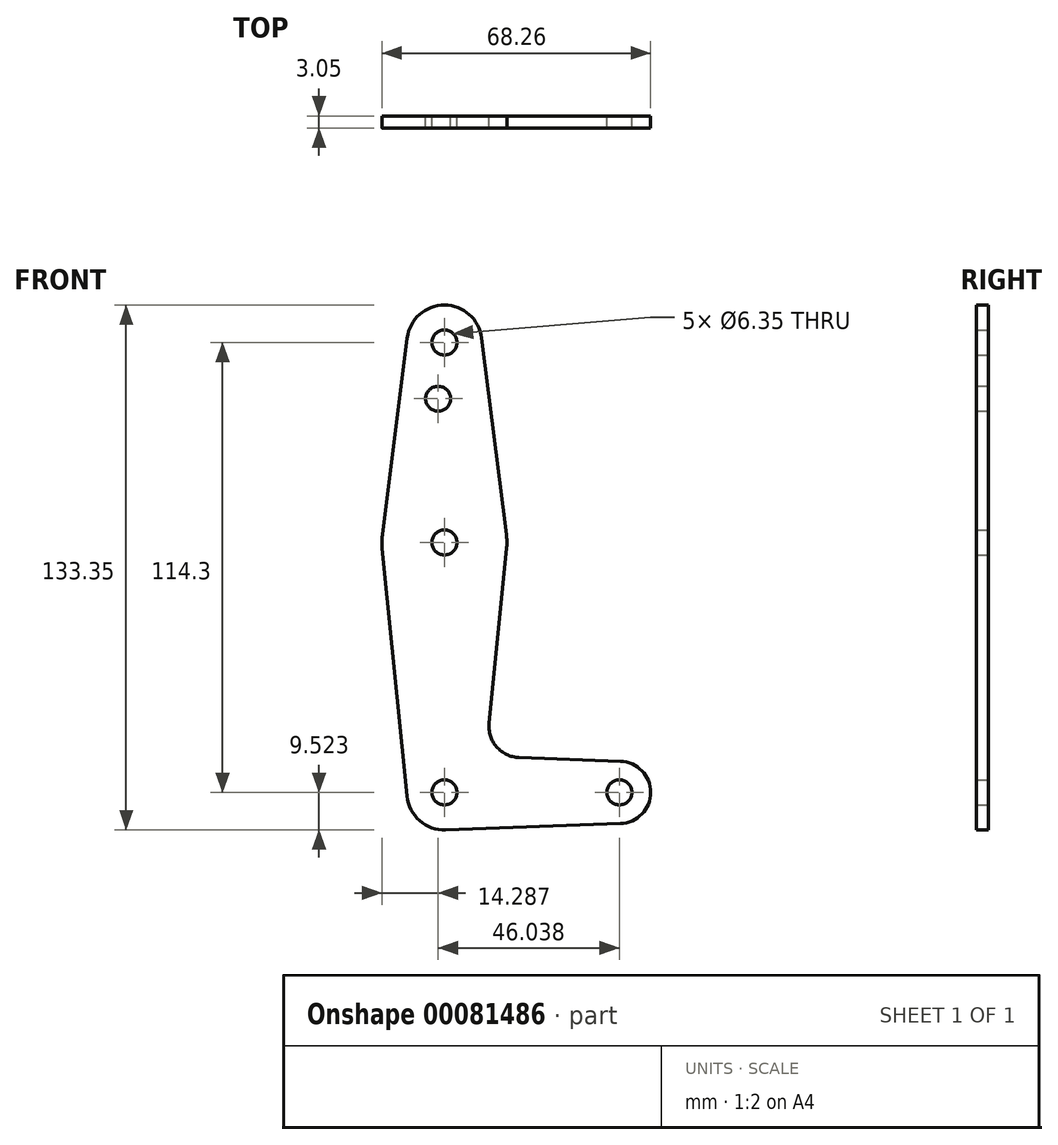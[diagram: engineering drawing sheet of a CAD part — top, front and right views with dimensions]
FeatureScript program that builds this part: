
annotation { "Feature Type Name" : "Feature", "Feature Type Description" : "" }
export const myFeature = defineFeature(function(context is Context, id is Id, definition is map)
    precondition{}
    {
        {
            var Q0;
            Q0=qCreatedBy(makeId("Front.planeOp"),FACE);
            var sketch = newSketch(context, id + "F0", { "sketchPlane" : qUnion([Q0])});
            skLineSegment(sketch, "E0", {"start": v(-60.13, 49.11) * mm, "end": v(-60.13, -65.19) * mm, "construction": true});
            skPoint(sketch, "E1.center.orphan", {"position": v(-60.13, -8.04) * mm});
            skCircle(sketch, "E2", {"center": v(-60.13, -1.69) * mm, "radius": 15.88 * mm});
            skCircle(sketch, "E3", {"center": v(-60.13, -65.19) * mm, "radius": 9.53 * mm});
            skLineSegment(sketch, "E4", {"start": v(-60.13, -65.19) * mm, "end": v(-15.68, -65.19) * mm, "construction": true});
            skCircle(sketch, "E5", {"center": v(-15.68, -65.19) * mm, "radius": 7.94 * mm});
            skPoint(sketch, "E6.start.orphan", {"position": v(-69.65, 49.11) * mm});
            skCircle(sketch, "E7", {"center": v(-60.13, 49.11) * mm, "radius": 9.53 * mm});
            skLineSegment(sketch, "E8", {"start": v(-69.58, 50.3) * mm, "end": v(-75.88, 0.3) * mm});
            skLineSegment(sketch, "E9", {"start": v(-75.92, -3.27) * mm, "end": v(-69.6, -66.14) * mm});
            skLineSegment(sketch, "E10", {"start": v(-50.67, 50.3) * mm, "end": v(-44.37, 0.3) * mm});
            skLineSegment(sketch, "E11", {"start": v(-44.33, -3.27) * mm, "end": v(-48.78, -47.6) * mm});
            skLineSegment(sketch, "E12", {"start": v(-41.16, -56.33) * mm, "end": v(-15.4, -57.25) * mm});
            skLineSegment(sketch, "E13", {"start": v(-59.78, -74.7) * mm, "end": v(-15.4, -73.12) * mm});
            skCircle(sketch, "E14", {"center": v(-60.13, 49.11) * mm, "radius": 3.18 * mm});
            skCircle(sketch, "E15", {"center": v(-60.13, -1.69) * mm, "radius": 3.18 * mm});
            skCircle(sketch, "E16", {"center": v(-60.13, -65.19) * mm, "radius": 3.18 * mm});
            skCircle(sketch, "E17", {"center": v(-15.68, -65.19) * mm, "radius": 3.18 * mm});
            skArc(sketch, "E18.filletArc", {"start": v(-48.78, -47.6) * mm, "mid": v(-46.86, -53.62) * mm, "end": v(-41.16, -56.33) * mm});
            skCircle(sketch, "E19", {"center": v(-61.71, 34.84) * mm, "radius": 3.18 * mm});
            skSolve(sketch);
        }
        {
            var Q0;
            Q0 = qSketchRegion(id + "F0", true);
            extrude(context, id + "F1", {"entities" : qUnion([Q0]), "depth" : 3.05 * mm});
        }
    });
